# Revit family: Кольцо 1000х990 с люком без замка КСП 10.9_10.10
name_source: partatom
category: Обобщенные модели
units: mm (PartAtom-declared; Revit-internal decimal feet)

## family parameters
Всегда вертикально = Да
Может служить основой для арматурных стержней = Нет
На основе рабочей плоскости = Нет
Общий = Нет
При загрузке вырезать с полостями = Нет
Размер круглого соединителя = Использовать диаметр
Сохранять ориентацию аннотаций = Нет
Тип детали = Нормальный
Точка принадлежности помещению = Нет

## types (1)
- Кольцо 1000х990 с люком без замка КСП 10.9/10.10
    ADSK_Масса = 843
    ADSK_Размер_Высота = 1010 мм
    ADSK_Размер_Диаметр = 1000 мм
    d1 = 7 мм
    h1 = 370 мм
    h2 = 305 мм
    t1 = 90 мм
    t2 = 80 мм
    Отметка по умолчанию = 0 мм
    вырез1 = Да
    вырез2 = Да
    диаметр_люка = 700 мм
    отступ_верх = 29 мм
    отступ_низ = 38 мм
    отступ_оси_люка_Х = 140 мм
    сужение_низ = 5 мм
    толщ_на_h1_расч = 12 мм
    толщ_на_h2_расч = 13 мм
    толщина_дна = 100 мм
    фаска = 10 мм
